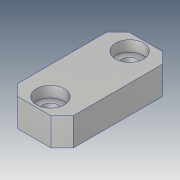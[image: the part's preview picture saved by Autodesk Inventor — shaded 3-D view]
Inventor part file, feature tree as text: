
AUTODESK INVENTOR PART (.ipt)
format: ipt  version: 2018.2 (Build 222227000, 227)  size: 111,104 bytes
history: native  units: mm
features: sketch x3, other x1, extrude x1, hole x1, chamfer x1
ambient origin geometry x8: Origin, YZ Plane, XZ Plane, XY Plane, X Axis, Y Axis, Z Axis, Center Point
bodies: Volumenkörper1 (feature_tree)
feature tree (7):
  other  "200-50-WHEEL-CONNECTOR-20MM-01.ipt"
  extrude  "Grundkörper"  Depth=10.0mm TaperAngle=0.0deg
  hole  "DIN7984_M5_Boh"  [1 undecoded]
  chamfer  "Fase_Allgemein"  [1 undecoded]
  sketch  "Skizze"
  sketch  "Skizze2"  dims[d0=10.0mm d1=10.0mm d2=0.0mm]
  sketch  "Skizze3"  dims[d3=5.5mm d4=6.0mm d5=10.0mm d6=3.9mm d7=90.0deg d8=8.0mm d9=20.594885mm d10=4.0mm d11=2.0mm d12=45.0deg]
note: 2 required parameter values undecoded (feature->parameter linkage not recoverable at this tier; creation-order binding heuristic only, values carry confidence <= 0.55)
